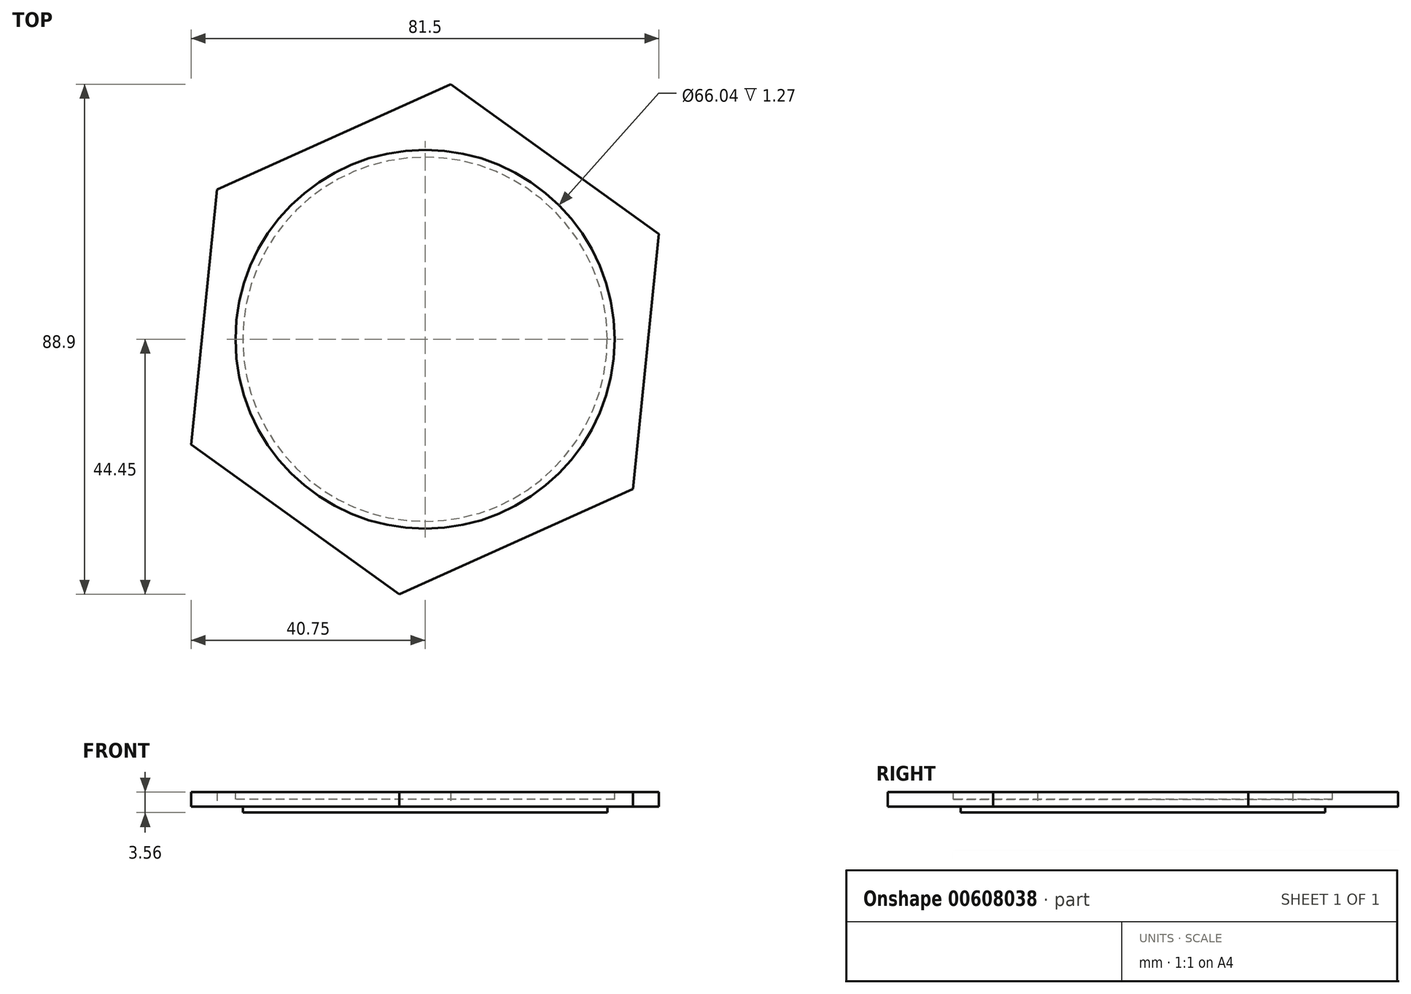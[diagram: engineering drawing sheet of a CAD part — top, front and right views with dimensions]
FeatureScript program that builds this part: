
annotation { "Feature Type Name" : "Feature", "Feature Type Description" : "" }
export const myFeature = defineFeature(function(context is Context, id is Id, definition is map)
    precondition{}
    {
        {
            var Q0;
            Q0=qCreatedBy(makeId("Top.planeOp"),FACE);
            var sketch = newSketch(context, id + "F0", { "sketchPlane" : qUnion([Q0])});
            skCircle(sketch, "E0.cCircle", {"center": v(0, 0) * mm, "radius": 38.7 * mm, "construction": true});
            skLineSegment(sketch, "E0.0", {"start": v(36.24, -26.12) * mm, "end": v(-4.5, -44.45) * mm});
            skLineSegment(sketch, "E0.1", {"start": v(-4.5, -44.45) * mm, "end": v(-40.75, -18.33) * mm});
            skLineSegment(sketch, "E0.2", {"start": v(-40.75, -18.33) * mm, "end": v(-36.24, 26.12) * mm});
            skLineSegment(sketch, "E0.3", {"start": v(-36.24, 26.12) * mm, "end": v(4.5, 44.45) * mm});
            skLineSegment(sketch, "E0.4", {"start": v(4.5, 44.45) * mm, "end": v(40.75, 18.33) * mm});
            skLineSegment(sketch, "E0.5", {"start": v(40.75, 18.33) * mm, "end": v(36.24, -26.12) * mm});
            skPoint(sketch, "E0.0.midPoint", {"position": v(15.87, -35.29) * mm});
            skLineSegment(sketch, "E1", {"start": v(4.5, 44.45) * mm, "end": v(-4.5, -44.45) * mm, "construction": true});
            skSolve(sketch);
        }
        {
            var Q0;
            Q0=makeQuery(id+"F0.imprint","IMPRINT",FACE,{"disambiguationData":[TD([[makeQuery(id+"F0.imprint","IMPRINT",EDGE,{"derivedFrom":sQuery(id+"F0.wireOp",EDGE,"E0.0")}),-1.0]])]});
            extrude(context, id + "F1", {"entities" : qUnion([Q0]), "depth" : 2.54 * mm, "offsetDistance" : 25.4 * mm});
        }
        {
            var Q0;
            Q0=makeQuery(id+"F1.opExtrude","CAP_FACE",FACE,{"disambiguationData":[OSD([sQuery(id+"F0.wireOp",EDGE,"E0.0"),sQuery(id+"F0.wireOp",EDGE,"E0.1"),sQuery(id+"F0.wireOp",EDGE,"E0.2"),sQuery(id+"F0.wireOp",EDGE,"E0.3"),sQuery(id+"F0.wireOp",EDGE,"E0.4"),sQuery(id+"F0.wireOp",EDGE,"E0.5")])],"isStart":false});
            var sketch = newSketch(context, id + "F2", { "sketchPlane" : qUnion([Q0])});
            skCircle(sketch, "E2", {"center": v(0, 0) * mm, "radius": 33.02 * mm});
            skSolve(sketch);
        }
        {
            var Q0;
            Q0 = qSketchRegion(id + "F2", true);
            extrude(context, id + "F3", {"entities" : qUnion([Q0]), "operationType" : NewBodyOperationType.REMOVE, "oppositeDirection" : true, "depth" : 1.27 * mm, "offsetDistance" : 25.4 * mm});
        }
        {
            var Q0;
            Q0=makeQuery(id+"F1.opExtrude","CAP_FACE",FACE,{"disambiguationData":[OSD([sQuery(id+"F0.wireOp",EDGE,"E0.0"),sQuery(id+"F0.wireOp",EDGE,"E0.1"),sQuery(id+"F0.wireOp",EDGE,"E0.2"),sQuery(id+"F0.wireOp",EDGE,"E0.3"),sQuery(id+"F0.wireOp",EDGE,"E0.4"),sQuery(id+"F0.wireOp",EDGE,"E0.5")])],"isStart":true});
            var sketch = newSketch(context, id + "F4", { "sketchPlane" : qUnion([Q0])});
            skCircle(sketch, "E3", {"center": v(0, 0) * mm, "radius": 31.75 * mm});
            skSolve(sketch);
        }
        {
            var Q0;
            Q0 = qSketchRegion(id + "F4", true);
            extrude(context, id + "F5", {"entities" : qUnion([Q0]), "operationType" : NewBodyOperationType.ADD, "depth" : 1.02 * mm, "offsetDistance" : 25.4 * mm});
        }
    });
